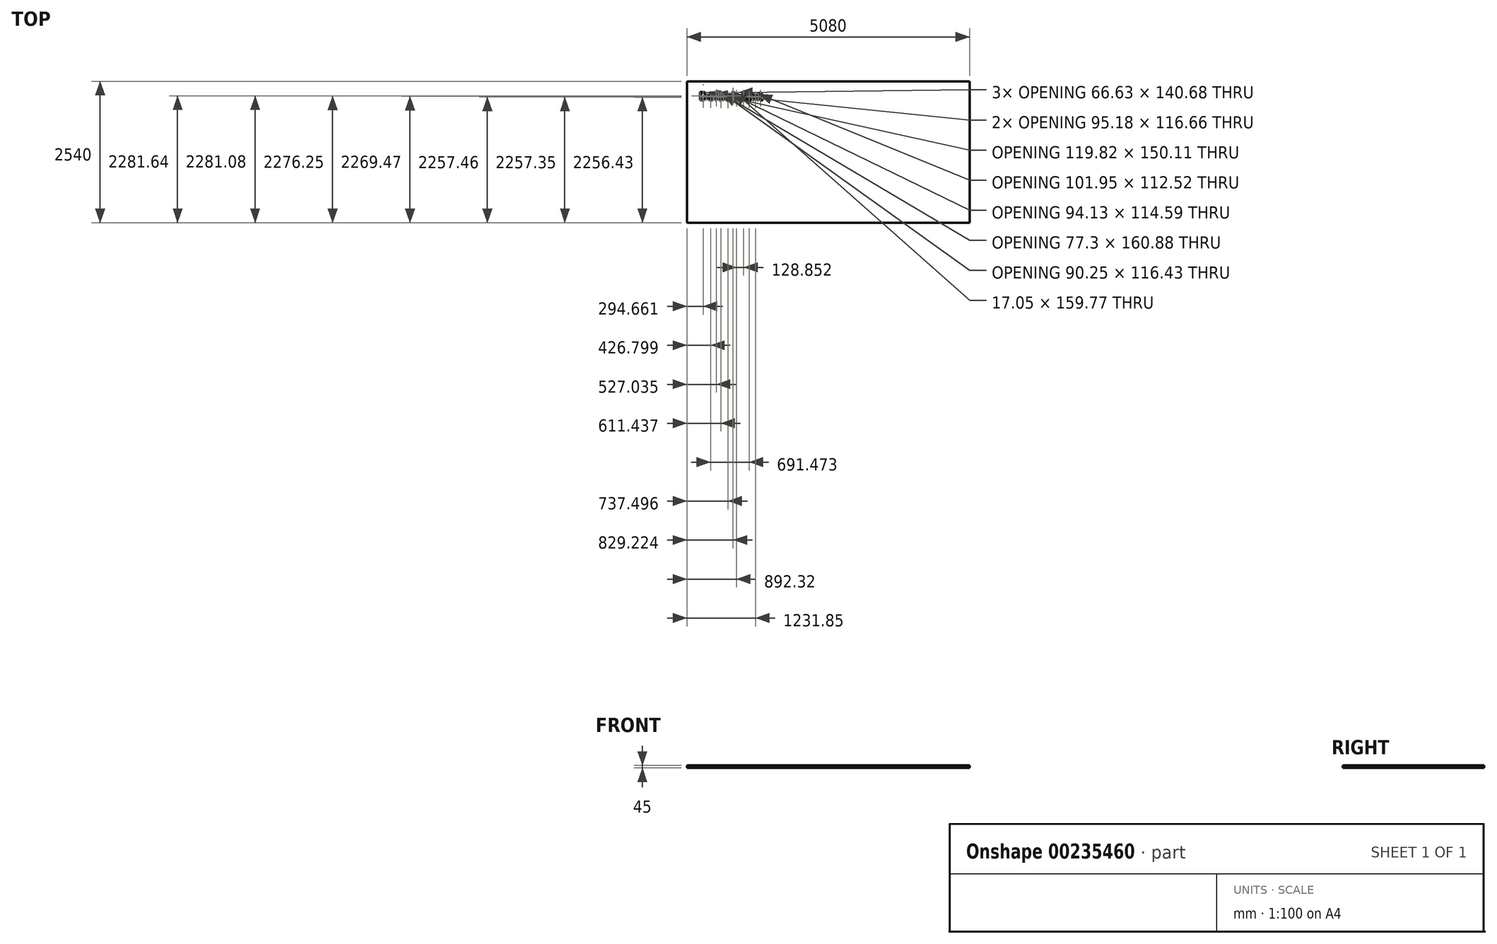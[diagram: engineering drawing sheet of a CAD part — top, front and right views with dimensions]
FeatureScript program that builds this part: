
annotation { "Feature Type Name" : "Feature", "Feature Type Description" : "" }
export const myFeature = defineFeature(function(context is Context, id is Id, definition is map)
    precondition{}
    {
        {
            var Q0;
            Q0=qCreatedBy(makeId("Top.planeOp"),FACE);
            var sketch = newSketch(context, id + "F0", { "sketchPlane" : qUnion([Q0])});
            skLineSegment(sketch, "E0.bottom", {"start": v(0, 0) * mm, "end": v(5080, 0) * mm});
            skLineSegment(sketch, "E0.top", {"start": v(0, 2540) * mm, "end": v(5080, 2540) * mm});
            skLineSegment(sketch, "E0.left", {"start": v(0, 0) * mm, "end": v(0, 2540) * mm});
            skLineSegment(sketch, "E0.right", {"start": v(5080, 0) * mm, "end": v(5080, 2540) * mm});
            skSolve(sketch);
        }
        {
            var Q0;
            Q0=makeQuery(id+"F0.imprint","IMPRINT",FACE,{"disambiguationData":[TD([[makeQuery(id+"F0.imprint","IMPRINT",EDGE,{"derivedFrom":sQuery(id+"F0.wireOp",EDGE,"E0.bottom")}),1.0]])]});
            extrude(context, id + "F1", {"entities" : qUnion([Q0]), "depth" : 20 * mm});
        }
        {
            var Q0;
            Q0=makeQuery(id+"F1.opExtrude","CAP_FACE",FACE,{"disambiguationData":[OSD([sQuery(id+"F0.wireOp",EDGE,"E0.bottom"),sQuery(id+"F0.wireOp",EDGE,"E0.top"),sQuery(id+"F0.wireOp",EDGE,"E0.left"),sQuery(id+"F0.wireOp",EDGE,"E0.right")])],"isStart":false});
            var sketch = newSketch(context, id + "F2", { "sketchPlane" : qUnion([Q0])});
            skText(sketch, "E1", { "text": "Default text", "fontName": "OpenSans-Regular.ttf"});
            const initialGuessF2  = {"E1": [0.21412, 2.2012, 1, 0, 0.15139]};
            skSetInitialGuess(sketch, initialGuessF2);
            skSolve(sketch);
        }
        {
            var Q0;
            Q0 = qSketchRegion(id + "F2", true);
            extrude(context, id + "F3", {"entities" : qUnion([Q0]), "operationType" : NewBodyOperationType.REMOVE, "oppositeDirection" : true, "depth" : 178 * mm});
        }
        {
            var Q0;
            {var subQ0=sQuery(id+"F0.wireOp",EDGE,"E0.top");var subQ1=sQuery(id+"F0.wireOp",EDGE,"E0.right");var subQ2=sQuery(id+"F0.wireOp",EDGE,"E0.bottom");var subQ3=sQuery(id+"F0.wireOp",EDGE,"E0.left");Q0=makeQuery(id+"F3.boolean.opBoolean","SPLIT",FACE,{"disambiguationData":[TD([makeQuery(id+"F1.opExtrude","SWEPT_FACE",FACE,{"disambiguationData":[OSD([subQ2])]})])],"derivedFrom":makeQuery(id+"F1.opExtrude","CAP_FACE",FACE,{"disambiguationData":[OSD([subQ2,subQ0,subQ3,subQ1])],"isStart":false})});}
            extrude(context, id + "F4", {"entities" : qUnion([Q0]), "operationType" : NewBodyOperationType.ADD, "depth" : 25 * mm, "offsetDistance" : 25 * mm});
        }
    });
